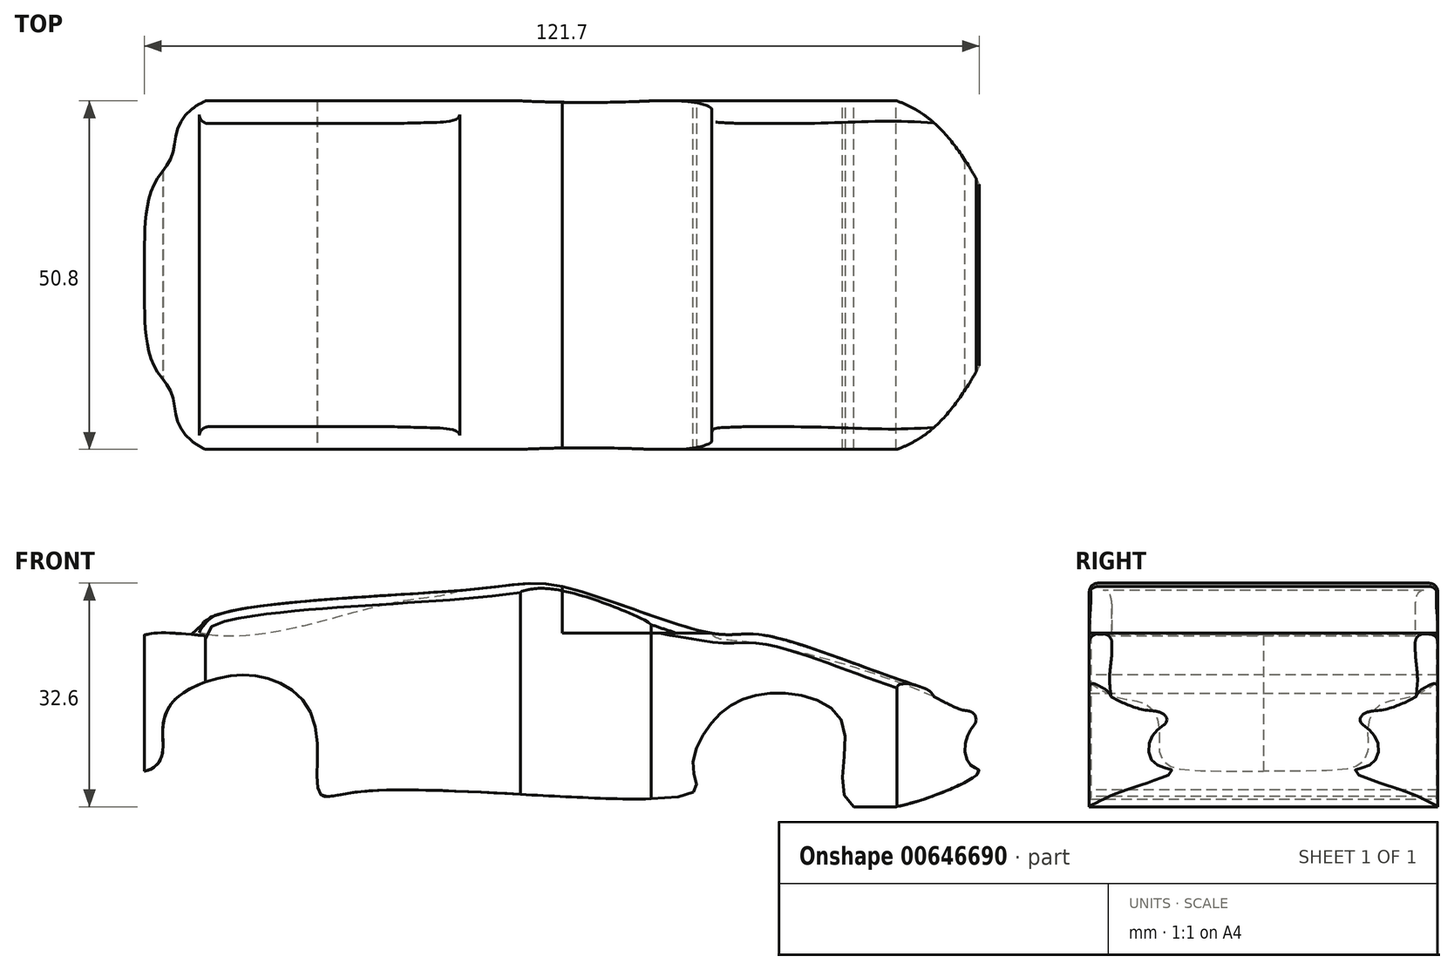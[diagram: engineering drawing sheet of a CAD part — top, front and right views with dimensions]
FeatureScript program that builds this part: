
annotation { "Feature Type Name" : "Feature", "Feature Type Description" : "" }
export const myFeature = defineFeature(function(context is Context, id is Id, definition is map)
    precondition{}
    {
        {
            var Q0;
            Q0=qCreatedBy(makeId("Top.planeOp"),FACE);
            var sketch = newSketch(context, id + "F0", { "sketchPlane" : qUnion([Q0])});
            skFitSpline(sketch, "E0", {"points": [v(-60.9, 0) * mm, v(-59.7, 12.78) * mm, v(-57, 17.15) * mm, v(-55.95, 21.66) * mm, v(-48.73, 26.47) * mm, v(-6.47, 25.42) * mm, v(22.86, 26.02) * mm, v(42.26, 26.62) * mm, v(55.2, 21.2) * mm, v(64.8, 3.46) * mm, v(64.94, 0) * mm], "startDerivative": vector(-1.03, 153.82) * mm, "endDerivative": vector(-8.14, -52.99) * mm});
            skFitSpline(sketch, "E1.MirrorCS", {"points": [v(-60.9, 0) * mm, v(-59.7, -12.78) * mm, v(-57, -17.15) * mm, v(-55.95, -21.66) * mm, v(-48.73, -26.47) * mm, v(-6.47, -25.42) * mm, v(22.86, -26.02) * mm, v(42.26, -26.62) * mm, v(55.2, -21.2) * mm, v(64.8, -3.46) * mm, v(64.94, 0) * mm], "startDerivative": vector(-1.03, -153.82) * mm, "endDerivative": vector(-8.14, 52.99) * mm});
            skSolve(sketch);
        }
        {
            var Q0;
            Q0=qCreatedBy(makeId("Front.planeOp"),FACE);
            var sketch = newSketch(context, id + "F1", { "sketchPlane" : qUnion([Q0])});
            skLineSegment(sketch, "E2.bottom", {"start": v(-68.32, 73.07) * mm, "end": v(69.18, 73.07) * mm});
            skLineSegment(sketch, "E2.top", {"start": v(-68.32, -10.65) * mm, "end": v(69.18, -10.65) * mm});
            skLineSegment(sketch, "E2.left", {"start": v(-68.32, 73.07) * mm, "end": v(-68.32, -10.65) * mm});
            skLineSegment(sketch, "E2.right", {"start": v(69.18, 73.07) * mm, "end": v(69.18, -10.65) * mm});
            skLineSegment(sketch, "E3", {"start": v(0, 25.3) * mm, "end": v(0, 32.11) * mm});
            skFitSpline(sketch, "E4.MirrorC", {"points": [v(60.75, 13.41) * mm, v(49.26, 18.48) * mm, v(28.81, 25.1) * mm, v(21.8, 25.3) * mm, v(0, 32.11) * mm, v(-12.86, 31.72) * mm, v(-52.2, 27.05) * mm, v(-52.98, 25.3) * mm, v(-63.1, 23.93) * mm, v(-63.3, 6.01) * mm, v(-58.83, 6.4) * mm, v(-58.24, 10.69) * mm, v(-56.88, 15.17) * mm, v(-50.45, 18.67) * mm, v(-42.86, 18.67) * mm, v(-36.23, 12.64) * mm, v(-35.46, 2.12) * mm, v(-28.44, 2.31) * mm, v(19.07, 2.12) * mm, v(19.07, 5.43) * mm, v(21.41, 11.86) * mm, v(26.48, 15.75) * mm, v(34.27, 16.34) * mm, v(41.08, 11.47) * mm, v(42.44, 0) * mm, v(60.75, 5.04) * mm, v(59.39, 6.2) * mm, v(59.2, 10.69) * mm, v(60.75, 13.41) * mm]});
            skLineSegment(sketch, "E5.MirrorCS", {"start": v(21.8, 25.3) * mm, "end": v(0, 25.3) * mm});
            skSolve(sketch);
        }
        {
            var Q0;
            Q0=qCreatedBy(makeId("Front.planeOp"),FACE);
            cPlane(context, id + "F2", {"entities" : qUnion([Q0]), "cplaneType" : CPlaneType.OFFSET, "offset" : 25.4 * mm, "width" : 152.4 * mm, "height" : 152.4 * mm});
        }
        {
            var Q0;
            {var subQ0=sQuery(id+"F1.wireOp",EDGE,"E3");Q0=makeQuery(id+"F1.imprint","IMPRINT",FACE,{"disambiguationData":[TD([[makeQuery(id+"F1.imprint","IMPRINT",EDGE,{"derivedFrom":subQ0}),1.0]])]});}
            extrude(context, id + "F3", {"entities" : qUnion([Q0]), "endBound" : BoundingType.SYMMETRIC, "depth" : 50.8 * mm, "offsetDistance" : 25.4 * mm});
        }
        {
            var Q0;
            {var subQ0=sQuery(id+"F1.wireOp",EDGE,"E3");Q0=makeQuery(id+"F1.imprint","IMPRINT",FACE,{"disambiguationData":[TD([[makeQuery(id+"F1.imprint","IMPRINT",EDGE,{"derivedFrom":subQ0}),-1.0]])]});}
            extrude(context, id + "F4", {"entities" : qUnion([Q0]), "endBound" : BoundingType.SYMMETRIC, "depth" : 50.8 * mm, "offsetDistance" : 25.4 * mm});
        }
        {
            var Q0;
            Q0=makeQuery(id+"F0.imprint","IMPRINT",FACE,{"disambiguationData":[TD([[makeQuery(id+"F0.imprint","IMPRINT",EDGE,{"derivedFrom":sQuery(id+"F0.wireOp",EDGE,"E0")}),-1.0]])]});
            extrude(context, id + "F5", {"entities" : qUnion([Q0]), "operationType" : NewBodyOperationType.INTERSECT, "depth" : 50.8 * mm, "offsetDistance" : 25.4 * mm});
        }
        {
            var Q0;
            Q0=qCreatedBy(id+"F2.planeOp",FACE);
            var sketch = newSketch(context, id + "F6", { "sketchPlane" : qUnion([Q0])});
            skFitSpline(sketch, "E6", {"points": [v(-14.29, 31.88) * mm, v(-24.36, 29.78) * mm, v(-53.09, 25.42) * mm, v(-58.2, 32.64) * mm, v(-12.78, 35.5) * mm, v(-14.29, 31.88) * mm]});
            skFitSpline(sketch, "E7", {"points": [v(60.6, 14.02) * mm, v(54.11, 16.04) * mm, v(27.74, 23.91) * mm, v(21.78, 25.3) * mm, v(30.08, 31.68) * mm, v(67.4, 19.34) * mm, v(60.6, 14.02) * mm]});
            skSolve(sketch);
        }
        {
            var Q0;
            Q0=makeQuery(id+"F6.imprint","IMPRINT",FACE,{"disambiguationData":[TD([[makeQuery(id+"F6.imprint","IMPRINT",EDGE,{"derivedFrom":sQuery(id+"F6.wireOp",EDGE,"E6")}),-1.0]])]});
            var Q1;
            Q1=makeQuery(id+"F6.imprint","IMPRINT",FACE,{"disambiguationData":[TD([[makeQuery(id+"F6.imprint","IMPRINT",EDGE,{"derivedFrom":sQuery(id+"F6.wireOp",EDGE,"E7")}),-1.0]])]});
            extrude(context, id + "F7", {"entities" : qUnion([Q0, Q1]), "operationType" : NewBodyOperationType.REMOVE, "oppositeDirection" : true, "depth" : 47.5 * mm, "offsetDistance" : 25.4 * mm, "hasSecondDirection" : true, "secondDirectionOppositeDirection" : true, "secondDirectionDepth" : 3.3 * mm});
        }
        {
            var Q0;
            Q0=makeQuery(id+"F5.boolean.opBoolean","INTERSECT",EDGE,{"derivedFrom":[makeQuery(id+"F4.opExtrude","SWEPT_FACE",FACE,{"disambiguationData":[OSD([sQuery(id+"F1.wireOp",EDGE,"E4.MirrorC")])]}),makeQuery(id+"F5.boolean.toolComplement.opBoolean","COPY",FACE,{"derivedFrom":makeQuery(id+"F5.opExtrude","SWEPT_FACE",FACE,{"disambiguationData":[OSD([sQuery(id+"F0.wireOp",EDGE,"E1.MirrorCS")])]})})]});
            var Q1;
            Q1=makeQuery(id+"F4.opExtrude","CAP_EDGE",EDGE,{"disambiguationData":[OSD([sQuery(id+"F1.wireOp",EDGE,"E4.MirrorC")])],"isStart":false});
            var Q2;
            {var subQ0=sQuery(id+"F1.wireOp",EDGE,"E5.MirrorCS");var subQ1=sQuery(id+"F1.wireOp",EDGE,"E4.MirrorC");Q2=makeQuery(id+"F5.boolean.opBoolean","SPLIT",EDGE,{"disambiguationData":[TD([makeQuery(id+"F3.opExtrude","CAP_FACE",FACE,{"disambiguationData":[OSD([sQuery(id+"F1.wireOp",EDGE,"E3"),subQ1,subQ0])],"isStart":false}),makeQuery(id+"F3.opExtrude","SWEPT_FACE",FACE,{"disambiguationData":[OSD([subQ1])]}),makeQuery(id+"F3.opExtrude","SWEPT_FACE",FACE,{"disambiguationData":[OSD([subQ0])]}),makeQuery(id+"F5.boolean.toolComplement.opBoolean","COPY",FACE,{"derivedFrom":makeQuery(id+"F5.opExtrude","SWEPT_FACE",FACE,{"disambiguationData":[OSD([sQuery(id+"F0.wireOp",EDGE,"E1.MirrorCS")])]})})])],"derivedFrom":makeQuery(id+"F3.opExtrude","CAP_EDGE",EDGE,{"disambiguationData":[OSD([subQ1])],"isStart":false})});}
            var Q3;
            {var subQ0=sQuery(id+"F1.wireOp",EDGE,"E4.MirrorC");Q3=makeQuery(id+"F7.boolean.opBoolean","INTERSECT",EDGE,{"derivedFrom":[makeQuery(id+"F5.boolean.opBoolean","COPY",FACE,{"disambiguationData":[TD([makeQuery(id+"F3.opExtrude","CAP_FACE",FACE,{"disambiguationData":[OSD([sQuery(id+"F1.wireOp",EDGE,"E3"),subQ0,sQuery(id+"F1.wireOp",EDGE,"E5.MirrorCS")])],"isStart":false}),makeQuery(id+"F3.opExtrude","SWEPT_FACE",FACE,{"disambiguationData":[OSD([subQ0])]})])],"derivedFrom":makeQuery(id+"F5.boolean.toolComplement.opBoolean","COPY",FACE,{"derivedFrom":makeQuery(id+"F5.opExtrude","SWEPT_FACE",FACE,{"disambiguationData":[OSD([sQuery(id+"F0.wireOp",EDGE,"E1.MirrorCS")])]})})}),makeQuery(id+"F7.opExtrude","SWEPT_FACE",FACE,{"disambiguationData":[OSD([sQuery(id+"F6.wireOp",EDGE,"E7")])]})]});}
            var Q4;
            {var subQ0=sQuery(id+"F1.wireOp",EDGE,"E5.MirrorCS");var subQ1=sQuery(id+"F0.wireOp",EDGE,"E0");var subQ2=sQuery(id+"F1.wireOp",EDGE,"E4.MirrorC");var subQ3=sQuery(id+"F1.wireOp",EDGE,"E3");var subQ4=sQuery(id+"F0.wireOp",EDGE,"E1.MirrorCS");Q4=makeQuery(id+"F7.boolean.opBoolean","INTERSECT",EDGE,{"derivedFrom":[makeQuery(id+"F5.boolean.opBoolean","SPLIT",FACE,{"disambiguationData":[TD([makeQuery(id+"F3.opExtrude","CAP_FACE",FACE,{"disambiguationData":[OSD([subQ3,subQ2,subQ0])],"isStart":true}),makeQuery(id+"F3.opExtrude","CAP_FACE",FACE,{"disambiguationData":[OSD([subQ3,subQ2,subQ0])],"isStart":false}),makeQuery(id+"F3.opExtrude","SWEPT_FACE",FACE,{"disambiguationData":[OSD([subQ0])]}),makeQuery(id+"F5.boolean.toolComplement.opBoolean","COPY",FACE,{"derivedFrom":makeQuery(id+"F5.opExtrude","SWEPT_FACE",FACE,{"disambiguationData":[OSD([subQ1])]})}),makeQuery(id+"F5.boolean.toolComplement.opBoolean","COPY",FACE,{"derivedFrom":makeQuery(id+"F5.opExtrude","CAP_FACE",FACE,{"disambiguationData":[OSD([subQ1,subQ4])],"isStart":true})}),makeQuery(id+"F5.boolean.toolComplement.opBoolean","COPY",FACE,{"derivedFrom":makeQuery(id+"F5.opExtrude","SWEPT_FACE",FACE,{"disambiguationData":[OSD([subQ4])]})})])],"derivedFrom":makeQuery(id+"F3.opExtrude","SWEPT_FACE",FACE,{"disambiguationData":[OSD([subQ2])]})}),makeQuery(id+"F7.opExtrude","SWEPT_FACE",FACE,{"disambiguationData":[OSD([sQuery(id+"F6.wireOp",EDGE,"E7")])]})]});}
            var Q5;
            {var subQ0=sQuery(id+"F1.wireOp",EDGE,"E4.MirrorC");Q5=makeQuery(id+"F7.boolean.opBoolean","INTERSECT",EDGE,{"derivedFrom":[makeQuery(id+"F5.boolean.opBoolean","COPY",FACE,{"disambiguationData":[TD([makeQuery(id+"F3.opExtrude","CAP_FACE",FACE,{"disambiguationData":[OSD([sQuery(id+"F1.wireOp",EDGE,"E3"),subQ0,sQuery(id+"F1.wireOp",EDGE,"E5.MirrorCS")])],"isStart":true}),makeQuery(id+"F3.opExtrude","SWEPT_FACE",FACE,{"disambiguationData":[OSD([subQ0])]})])],"derivedFrom":makeQuery(id+"F5.boolean.toolComplement.opBoolean","COPY",FACE,{"derivedFrom":makeQuery(id+"F5.opExtrude","SWEPT_FACE",FACE,{"disambiguationData":[OSD([sQuery(id+"F0.wireOp",EDGE,"E0")])]})})}),makeQuery(id+"F7.opExtrude","SWEPT_FACE",FACE,{"disambiguationData":[OSD([sQuery(id+"F6.wireOp",EDGE,"E7")])]})]});}
            var Q6;
            {var subQ0=sQuery(id+"F1.wireOp",EDGE,"E5.MirrorCS");var subQ1=sQuery(id+"F1.wireOp",EDGE,"E4.MirrorC");Q6=makeQuery(id+"F5.boolean.opBoolean","SPLIT",EDGE,{"disambiguationData":[TD([makeQuery(id+"F3.opExtrude","CAP_FACE",FACE,{"disambiguationData":[OSD([sQuery(id+"F1.wireOp",EDGE,"E3"),subQ1,subQ0])],"isStart":true}),makeQuery(id+"F3.opExtrude","SWEPT_FACE",FACE,{"disambiguationData":[OSD([subQ1])]}),makeQuery(id+"F3.opExtrude","SWEPT_FACE",FACE,{"disambiguationData":[OSD([subQ0])]}),makeQuery(id+"F5.boolean.toolComplement.opBoolean","COPY",FACE,{"derivedFrom":makeQuery(id+"F5.opExtrude","SWEPT_FACE",FACE,{"disambiguationData":[OSD([sQuery(id+"F0.wireOp",EDGE,"E0")])]})})])],"derivedFrom":makeQuery(id+"F3.opExtrude","CAP_EDGE",EDGE,{"disambiguationData":[OSD([subQ1])],"isStart":true})});}
            var Q7;
            Q7=makeQuery(id+"F4.opExtrude","CAP_EDGE",EDGE,{"disambiguationData":[OSD([sQuery(id+"F1.wireOp",EDGE,"E4.MirrorC")])],"isStart":true});
            var Q8;
            Q8=makeQuery(id+"F5.boolean.opBoolean","INTERSECT",EDGE,{"derivedFrom":[makeQuery(id+"F4.opExtrude","SWEPT_FACE",FACE,{"disambiguationData":[OSD([sQuery(id+"F1.wireOp",EDGE,"E4.MirrorC")])]}),makeQuery(id+"F5.boolean.toolComplement.opBoolean","COPY",FACE,{"derivedFrom":makeQuery(id+"F5.opExtrude","SWEPT_FACE",FACE,{"disambiguationData":[OSD([sQuery(id+"F0.wireOp",EDGE,"E0")])]})})]});
            var Q9;
            {var subQ0=sQuery(id+"F1.wireOp",EDGE,"E4.MirrorC");Q9=makeQuery(id+"F5.boolean.opBoolean","SPLIT",EDGE,{"disambiguationData":[TD([makeQuery(id+"F3.opExtrude","CAP_FACE",FACE,{"disambiguationData":[OSD([sQuery(id+"F1.wireOp",EDGE,"E3"),subQ0,sQuery(id+"F1.wireOp",EDGE,"E5.MirrorCS")])],"isStart":true}),makeQuery(id+"F3.opExtrude","SWEPT_FACE",FACE,{"disambiguationData":[OSD([subQ0])]}),makeQuery(id+"F5.boolean.toolComplement.opBoolean","COPY",FACE,{"derivedFrom":makeQuery(id+"F5.opExtrude","SWEPT_FACE",FACE,{"disambiguationData":[OSD([sQuery(id+"F0.wireOp",EDGE,"E0")])]})})]),OD(0.0)],"derivedFrom":makeQuery(id+"F3.opExtrude","CAP_EDGE",EDGE,{"disambiguationData":[OSD([subQ0])],"isStart":true})});}
            var Q10;
            Q10=makeQuery(id+"F5.boolean.opBoolean","INTERSECT",EDGE,{"disambiguationData":[OD(1.0)],"derivedFrom":[makeQuery(id+"F3.opExtrude","SWEPT_FACE",FACE,{"disambiguationData":[OSD([sQuery(id+"F1.wireOp",EDGE,"E4.MirrorC")])]}),makeQuery(id+"F5.boolean.toolComplement.opBoolean","COPY",FACE,{"derivedFrom":makeQuery(id+"F5.opExtrude","SWEPT_FACE",FACE,{"disambiguationData":[OSD([sQuery(id+"F0.wireOp",EDGE,"E0")])]})})]});
            var Q11;
            Q11=makeQuery(id+"F5.boolean.opBoolean","INTERSECT",EDGE,{"disambiguationData":[OD(1.0)],"derivedFrom":[makeQuery(id+"F3.opExtrude","SWEPT_FACE",FACE,{"disambiguationData":[OSD([sQuery(id+"F1.wireOp",EDGE,"E4.MirrorC")])]}),makeQuery(id+"F5.boolean.toolComplement.opBoolean","COPY",FACE,{"derivedFrom":makeQuery(id+"F5.opExtrude","SWEPT_FACE",FACE,{"disambiguationData":[OSD([sQuery(id+"F0.wireOp",EDGE,"E1.MirrorCS")])]})})]});
            var Q12;
            {var subQ0=sQuery(id+"F1.wireOp",EDGE,"E4.MirrorC");Q12=makeQuery(id+"F5.boolean.opBoolean","SPLIT",EDGE,{"disambiguationData":[TD([makeQuery(id+"F3.opExtrude","CAP_FACE",FACE,{"disambiguationData":[OSD([sQuery(id+"F1.wireOp",EDGE,"E3"),subQ0,sQuery(id+"F1.wireOp",EDGE,"E5.MirrorCS")])],"isStart":false}),makeQuery(id+"F3.opExtrude","SWEPT_FACE",FACE,{"disambiguationData":[OSD([subQ0])]}),makeQuery(id+"F5.boolean.toolComplement.opBoolean","COPY",FACE,{"derivedFrom":makeQuery(id+"F5.opExtrude","SWEPT_FACE",FACE,{"disambiguationData":[OSD([sQuery(id+"F0.wireOp",EDGE,"E1.MirrorCS")])]})})]),OD(0.0)],"derivedFrom":makeQuery(id+"F3.opExtrude","CAP_EDGE",EDGE,{"disambiguationData":[OSD([subQ0])],"isStart":false})});}
            var Q13;
            Q13=makeQuery(id+"F5.boolean.opBoolean","INTERSECT",EDGE,{"disambiguationData":[OD(0.0)],"derivedFrom":[makeQuery(id+"F3.opExtrude","SWEPT_FACE",FACE,{"disambiguationData":[OSD([sQuery(id+"F1.wireOp",EDGE,"E4.MirrorC")])]}),makeQuery(id+"F5.boolean.toolComplement.opBoolean","COPY",FACE,{"derivedFrom":makeQuery(id+"F5.opExtrude","SWEPT_FACE",FACE,{"disambiguationData":[OSD([sQuery(id+"F0.wireOp",EDGE,"E1.MirrorCS")])]})})]});
            var Q14;
            Q14=makeQuery(id+"F5.boolean.opBoolean","INTERSECT",EDGE,{"disambiguationData":[OD(0.0)],"derivedFrom":[makeQuery(id+"F3.opExtrude","SWEPT_FACE",FACE,{"disambiguationData":[OSD([sQuery(id+"F1.wireOp",EDGE,"E4.MirrorC")])]}),makeQuery(id+"F5.boolean.toolComplement.opBoolean","COPY",FACE,{"derivedFrom":makeQuery(id+"F5.opExtrude","SWEPT_FACE",FACE,{"disambiguationData":[OSD([sQuery(id+"F0.wireOp",EDGE,"E0")])]})})]});
            fillet(context, id + "F8", {"entities" : qUnion([Q0, Q1, Q2, Q3, Q4, Q5, Q6, Q7, Q8, Q9, Q10, Q11, Q12, Q13, Q14]), "radius" : 1.27 * mm, "tangentPropagation" : true, "allowEdgeOverflow" : false});
        }
        {
            var Q0;
            {var subQ0=sQuery(id+"F1.wireOp",EDGE,"E5.MirrorCS");var subQ1=sQuery(id+"F0.wireOp",EDGE,"E0");var subQ2=sQuery(id+"F1.wireOp",EDGE,"E4.MirrorC");var subQ3=sQuery(id+"F1.wireOp",EDGE,"E3");var subQ4=sQuery(id+"F0.wireOp",EDGE,"E1.MirrorCS");Q0=makeQuery(id+"F7.boolean.opBoolean","INTERSECT",EDGE,{"derivedFrom":[makeQuery(id+"F5.boolean.opBoolean","SPLIT",FACE,{"disambiguationData":[TD([makeQuery(id+"F3.opExtrude","CAP_FACE",FACE,{"disambiguationData":[OSD([subQ3,subQ2,subQ0])],"isStart":true}),makeQuery(id+"F3.opExtrude","CAP_FACE",FACE,{"disambiguationData":[OSD([subQ3,subQ2,subQ0])],"isStart":false}),makeQuery(id+"F3.opExtrude","SWEPT_FACE",FACE,{"disambiguationData":[OSD([subQ0])]}),makeQuery(id+"F5.boolean.toolComplement.opBoolean","COPY",FACE,{"derivedFrom":makeQuery(id+"F5.opExtrude","SWEPT_FACE",FACE,{"disambiguationData":[OSD([subQ1])]})}),makeQuery(id+"F5.boolean.toolComplement.opBoolean","COPY",FACE,{"derivedFrom":makeQuery(id+"F5.opExtrude","CAP_FACE",FACE,{"disambiguationData":[OSD([subQ1,subQ4])],"isStart":true})}),makeQuery(id+"F5.boolean.toolComplement.opBoolean","COPY",FACE,{"derivedFrom":makeQuery(id+"F5.opExtrude","SWEPT_FACE",FACE,{"disambiguationData":[OSD([subQ4])]})})])],"derivedFrom":makeQuery(id+"F3.opExtrude","SWEPT_FACE",FACE,{"disambiguationData":[OSD([subQ2])]})}),makeQuery(id+"F7.opExtrude","CAP_FACE",FACE,{"disambiguationData":[OSD([sQuery(id+"F6.wireOp",EDGE,"E7")])],"isStart":true})]});}
            var Q1;
            {var subQ0=sQuery(id+"F1.wireOp",EDGE,"E5.MirrorCS");var subQ1=sQuery(id+"F0.wireOp",EDGE,"E0");var subQ2=sQuery(id+"F1.wireOp",EDGE,"E4.MirrorC");var subQ3=sQuery(id+"F1.wireOp",EDGE,"E3");var subQ4=sQuery(id+"F0.wireOp",EDGE,"E1.MirrorCS");Q1=makeQuery(id+"F7.boolean.opBoolean","INTERSECT",EDGE,{"derivedFrom":[makeQuery(id+"F5.boolean.opBoolean","SPLIT",FACE,{"disambiguationData":[TD([makeQuery(id+"F3.opExtrude","CAP_FACE",FACE,{"disambiguationData":[OSD([subQ3,subQ2,subQ0])],"isStart":true}),makeQuery(id+"F3.opExtrude","CAP_FACE",FACE,{"disambiguationData":[OSD([subQ3,subQ2,subQ0])],"isStart":false}),makeQuery(id+"F3.opExtrude","SWEPT_FACE",FACE,{"disambiguationData":[OSD([subQ0])]}),makeQuery(id+"F5.boolean.toolComplement.opBoolean","COPY",FACE,{"derivedFrom":makeQuery(id+"F5.opExtrude","SWEPT_FACE",FACE,{"disambiguationData":[OSD([subQ1])]})}),makeQuery(id+"F5.boolean.toolComplement.opBoolean","COPY",FACE,{"derivedFrom":makeQuery(id+"F5.opExtrude","CAP_FACE",FACE,{"disambiguationData":[OSD([subQ1,subQ4])],"isStart":true})}),makeQuery(id+"F5.boolean.toolComplement.opBoolean","COPY",FACE,{"derivedFrom":makeQuery(id+"F5.opExtrude","SWEPT_FACE",FACE,{"disambiguationData":[OSD([subQ4])]})})])],"derivedFrom":makeQuery(id+"F3.opExtrude","SWEPT_FACE",FACE,{"disambiguationData":[OSD([subQ2])]})}),makeQuery(id+"F7.opExtrude","CAP_FACE",FACE,{"disambiguationData":[OSD([sQuery(id+"F6.wireOp",EDGE,"E7")])],"isStart":false})]});}
            var Q2;
            {var subQ0=sQuery(id+"F1.wireOp",EDGE,"E5.MirrorCS");var subQ1=sQuery(id+"F1.wireOp",EDGE,"E4.MirrorC");var subQ2=sQuery(id+"F1.wireOp",EDGE,"E3");Q2=makeQuery(id+"F7.boolean.opBoolean","INTERSECT",EDGE,{"derivedFrom":[makeQuery(id+"F5.boolean.opBoolean","SPLIT",FACE,{"disambiguationData":[TD([makeQuery(id+"F3.opExtrude","SWEPT_FACE",FACE,{"disambiguationData":[OSD([subQ2])]}),makeQuery(id+"F3.opExtrude","CAP_FACE",FACE,{"disambiguationData":[OSD([subQ2,subQ1,subQ0])],"isStart":true}),makeQuery(id+"F3.opExtrude","CAP_FACE",FACE,{"disambiguationData":[OSD([subQ2,subQ1,subQ0])],"isStart":false}),makeQuery(id+"F5.boolean.toolComplement.opBoolean","COPY",FACE,{"derivedFrom":makeQuery(id+"F5.opExtrude","SWEPT_FACE",FACE,{"disambiguationData":[OSD([sQuery(id+"F0.wireOp",EDGE,"E0")])]})}),makeQuery(id+"F5.boolean.toolComplement.opBoolean","COPY",FACE,{"derivedFrom":makeQuery(id+"F5.opExtrude","SWEPT_FACE",FACE,{"disambiguationData":[OSD([sQuery(id+"F0.wireOp",EDGE,"E1.MirrorCS")])]})})])],"derivedFrom":makeQuery(id+"F3.opExtrude","SWEPT_FACE",FACE,{"disambiguationData":[OSD([subQ1])]})}),makeQuery(id+"F7.opExtrude","CAP_FACE",FACE,{"disambiguationData":[OSD([sQuery(id+"F6.wireOp",EDGE,"E6")])],"isStart":false})]});}
            var Q3;
            {var subQ0=sQuery(id+"F1.wireOp",EDGE,"E5.MirrorCS");var subQ1=sQuery(id+"F1.wireOp",EDGE,"E4.MirrorC");var subQ2=sQuery(id+"F1.wireOp",EDGE,"E3");Q3=makeQuery(id+"F7.boolean.opBoolean","INTERSECT",EDGE,{"derivedFrom":[makeQuery(id+"F5.boolean.opBoolean","SPLIT",FACE,{"disambiguationData":[TD([makeQuery(id+"F3.opExtrude","SWEPT_FACE",FACE,{"disambiguationData":[OSD([subQ2])]}),makeQuery(id+"F3.opExtrude","CAP_FACE",FACE,{"disambiguationData":[OSD([subQ2,subQ1,subQ0])],"isStart":true}),makeQuery(id+"F3.opExtrude","CAP_FACE",FACE,{"disambiguationData":[OSD([subQ2,subQ1,subQ0])],"isStart":false}),makeQuery(id+"F5.boolean.toolComplement.opBoolean","COPY",FACE,{"derivedFrom":makeQuery(id+"F5.opExtrude","SWEPT_FACE",FACE,{"disambiguationData":[OSD([sQuery(id+"F0.wireOp",EDGE,"E0")])]})}),makeQuery(id+"F5.boolean.toolComplement.opBoolean","COPY",FACE,{"derivedFrom":makeQuery(id+"F5.opExtrude","SWEPT_FACE",FACE,{"disambiguationData":[OSD([sQuery(id+"F0.wireOp",EDGE,"E1.MirrorCS")])]})})])],"derivedFrom":makeQuery(id+"F3.opExtrude","SWEPT_FACE",FACE,{"disambiguationData":[OSD([subQ1])]})}),makeQuery(id+"F7.opExtrude","CAP_FACE",FACE,{"disambiguationData":[OSD([sQuery(id+"F6.wireOp",EDGE,"E6")])],"isStart":true})]});}
            fillet(context, id + "F9", {"entities" : qUnion([Q0, Q1, Q2, Q3]), "radius" : 1.27 * mm, "tangentPropagation" : true, "allowEdgeOverflow" : false});
        }
    });
